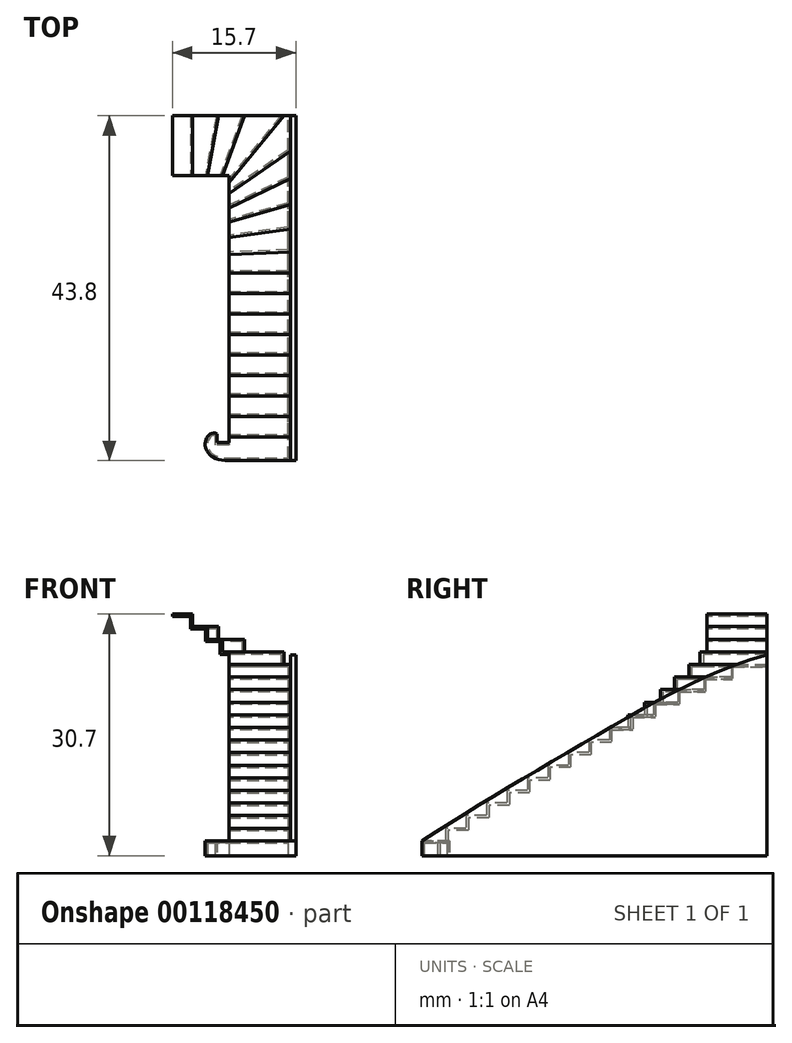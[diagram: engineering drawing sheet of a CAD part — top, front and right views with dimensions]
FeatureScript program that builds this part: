
annotation { "Feature Type Name" : "Feature", "Feature Type Description" : "" }
export const myFeature = defineFeature(function(context is Context, id is Id, definition is map)
    precondition{}
    {
        {
            var Q0;
            Q0=qCreatedBy(makeId("Top.planeOp"),FACE);
            var sketch = newSketch(context, id + "F0", { "sketchPlane" : qUnion([Q0])});
            skLineSegment(sketch, "E0", {"start": v(0, 0) * mm, "end": v(0, -0.9) * mm});
            skLineSegment(sketch, "E1", {"start": v(0, -0.9) * mm, "end": v(0, -2.3) * mm});
            skLineSegment(sketch, "E2", {"start": v(0, -2.3) * mm, "end": v(0, -4.1) * mm});
            skLineSegment(sketch, "E3", {"start": v(0, -4.1) * mm, "end": v(0, -5.9) * mm});
            skLineSegment(sketch, "E4", {"start": v(0, -5.9) * mm, "end": v(0, -7.9) * mm});
            skLineSegment(sketch, "E5", {"start": v(0, -7.9) * mm, "end": v(0, -10) * mm});
            skLineSegment(sketch, "E6", {"start": v(0, -10) * mm, "end": v(0, -12.4) * mm});
            skLineSegment(sketch, "E7", {"start": v(0, -12.4) * mm, "end": v(0, -15) * mm});
            skLineSegment(sketch, "E8", {"start": v(0, -15) * mm, "end": v(7.8, -15) * mm});
            skLineSegment(sketch, "E9", {"start": v(7.8, -15) * mm, "end": v(7.8, -12.4) * mm});
            skLineSegment(sketch, "E10", {"start": v(7.8, -12.4) * mm, "end": v(7.8, -9.7) * mm});
            skLineSegment(sketch, "E11", {"start": v(7.8, -9.7) * mm, "end": v(7.8, -6.8) * mm});
            skLineSegment(sketch, "E12", {"start": v(7.8, -6.8) * mm, "end": v(7.8, -3.7) * mm});
            skLineSegment(sketch, "E13", {"start": v(7.8, -3.7) * mm, "end": v(7.8, -0.4) * mm});
            skLineSegment(sketch, "E14", {"start": v(7.8, -0.4) * mm, "end": v(7.8, 3.1) * mm});
            skLineSegment(sketch, "E15", {"start": v(7.8, 3.1) * mm, "end": v(7.8, 7.6) * mm});
            skLineSegment(sketch, "E16", {"start": v(7.8, 7.6) * mm, "end": v(7, 7.6) * mm});
            skLineSegment(sketch, "E17", {"start": v(7, 7.6) * mm, "end": v(2, 7.6) * mm});
            skLineSegment(sketch, "E18", {"start": v(2, 7.6) * mm, "end": v(-1.3, 7.6) * mm});
            skLineSegment(sketch, "E19", {"start": v(-1.3, 7.6) * mm, "end": v(-4.6, 7.6) * mm});
            skLineSegment(sketch, "E20", {"start": v(-4.6, 7.6) * mm, "end": v(-7.2, 7.6) * mm});
            skLineSegment(sketch, "E21", {"start": v(-7.2, 7.6) * mm, "end": v(-7.2, 0) * mm});
            skLineSegment(sketch, "E22", {"start": v(-7.2, 0) * mm, "end": v(-4.6, 0) * mm});
            skLineSegment(sketch, "E23", {"start": v(-4.6, 0) * mm, "end": v(-2.7, 0) * mm});
            skLineSegment(sketch, "E24", {"start": v(-2.7, 0) * mm, "end": v(-0.8, 0) * mm});
            skLineSegment(sketch, "E25", {"start": v(-0.8, 0) * mm, "end": v(0, 0) * mm});
            skLineSegment(sketch, "E26.0.1.0", {"start": v(0, -17.6) * mm, "end": v(7.8, -17.6) * mm});
            skLineSegment(sketch, "E26.0.1.1", {"start": v(7.8, -17.6) * mm, "end": v(7.8, -15) * mm});
            skLineSegment(sketch, "E26.0.1.2", {"start": v(0, -15) * mm, "end": v(0, -17.6) * mm});
            skLineSegment(sketch, "E26.0.2.0", {"start": v(0, -20.2) * mm, "end": v(7.8, -20.2) * mm});
            skLineSegment(sketch, "E26.0.2.1", {"start": v(7.8, -20.2) * mm, "end": v(7.8, -17.6) * mm});
            skLineSegment(sketch, "E26.0.2.2", {"start": v(0, -17.6) * mm, "end": v(0, -20.2) * mm});
            skLineSegment(sketch, "E26.0.3.0", {"start": v(0, -22.8) * mm, "end": v(7.8, -22.8) * mm});
            skLineSegment(sketch, "E26.0.3.1", {"start": v(7.8, -22.8) * mm, "end": v(7.8, -20.2) * mm});
            skLineSegment(sketch, "E26.0.3.2", {"start": v(0, -20.2) * mm, "end": v(0, -22.8) * mm});
            skLineSegment(sketch, "E26.0.4.0", {"start": v(0, -25.4) * mm, "end": v(7.8, -25.4) * mm});
            skLineSegment(sketch, "E26.0.4.1", {"start": v(7.8, -25.4) * mm, "end": v(7.8, -22.8) * mm});
            skLineSegment(sketch, "E26.0.4.2", {"start": v(0, -22.8) * mm, "end": v(0, -25.4) * mm});
            skLineSegment(sketch, "E26.0.5.0", {"start": v(0, -28) * mm, "end": v(7.8, -28) * mm});
            skLineSegment(sketch, "E26.0.5.1", {"start": v(7.8, -28) * mm, "end": v(7.8, -25.4) * mm});
            skLineSegment(sketch, "E26.0.5.2", {"start": v(0, -25.4) * mm, "end": v(0, -28) * mm});
            skLineSegment(sketch, "E26.0.6.0", {"start": v(0, -30.6) * mm, "end": v(7.8, -30.6) * mm});
            skLineSegment(sketch, "E26.0.6.1", {"start": v(7.8, -30.6) * mm, "end": v(7.8, -28) * mm});
            skLineSegment(sketch, "E26.0.6.2", {"start": v(0, -28) * mm, "end": v(0, -30.6) * mm});
            skLineSegment(sketch, "E26.0.7.0", {"start": v(0, -33.2) * mm, "end": v(7.8, -33.2) * mm});
            skLineSegment(sketch, "E26.0.7.1", {"start": v(7.8, -33.2) * mm, "end": v(7.8, -30.6) * mm});
            skLineSegment(sketch, "E26.0.7.2", {"start": v(0, -30.6) * mm, "end": v(0, -33.2) * mm});
            skLineSegment(sketch, "E26.0.8.0", {"start": v(0, -36.2) * mm, "end": v(7.8, -36.2) * mm});
            skLineSegment(sketch, "E26.0.8.1", {"start": v(7.8, -36.2) * mm, "end": v(7.8, -33.2) * mm});
            skLineSegment(sketch, "E26.0.8.2", {"start": v(0, -33.2) * mm, "end": v(0, -36.2) * mm});
            skLineSegment(sketch, "E26.direction2", {"start": v(0, -15) * mm, "end": v(0, -17.6) * mm, "construction": true});
            skLineSegment(sketch, "E27", {"start": v(7.8, -12.4) * mm, "end": v(0, -12.4) * mm});
            skLineSegment(sketch, "E28", {"start": v(7.8, -9.7) * mm, "end": v(0, -10) * mm});
            skLineSegment(sketch, "E29", {"start": v(7.8, -6.8) * mm, "end": v(0, -7.9) * mm});
            skLineSegment(sketch, "E30", {"start": v(7.8, -3.7) * mm, "end": v(0, -5.9) * mm});
            skLineSegment(sketch, "E31", {"start": v(7.8, -0.4) * mm, "end": v(0, -4.1) * mm});
            skLineSegment(sketch, "E32", {"start": v(7.8, 3.1) * mm, "end": v(0, -2.3) * mm});
            skLineSegment(sketch, "E33", {"start": v(7, 7.6) * mm, "end": v(0, -0.9) * mm});
            skLineSegment(sketch, "E34", {"start": v(2, 7.6) * mm, "end": v(-0.8, 0) * mm});
            skLineSegment(sketch, "E35", {"start": v(-1.3, 7.6) * mm, "end": v(-2.7, 0) * mm});
            skLineSegment(sketch, "E36", {"start": v(-4.6, 7.6) * mm, "end": v(-4.6, 0) * mm});
            skLineSegment(sketch, "E37.bottom", {"start": v(0, -33.2) * mm, "end": v(-1.5, -33.2) * mm, "construction": true});
            skLineSegment(sketch, "E37.top", {"start": v(0, -33.9) * mm, "end": v(-1.5, -33.9) * mm});
            skLineSegment(sketch, "E37.left", {"start": v(0, -33.2) * mm, "end": v(0, -33.9) * mm});
            skLineSegment(sketch, "E37.right", {"start": v(-1.5, -33.2) * mm, "end": v(-1.5, -33.9) * mm});
            skLineSegment(sketch, "E38.bottom", {"start": v(-1.5, -33.2) * mm, "end": v(0, -33.2) * mm, "construction": true});
            skLineSegment(sketch, "E38.top", {"start": v(-1.5, -32.8) * mm, "end": v(0, -32.8) * mm, "construction": true});
            skLineSegment(sketch, "E38.left", {"start": v(-1.5, -33.2) * mm, "end": v(-1.5, -32.8) * mm});
            skLineSegment(sketch, "E38.right", {"start": v(0, -33.2) * mm, "end": v(0, -32.8) * mm, "construction": true});
            skLineSegment(sketch, "E39", {"start": v(0, -33.9) * mm, "end": v(-3, -33.9) * mm, "construction": true});
            skFitSpline(sketch, "E40", {"points": [v(-1.5, -32.8) * mm, v(-3, -33.9) * mm, v(0, -36.2) * mm], "startDerivative": vector(-5.92, 2.61) * mm, "endDerivative": vector(11.96, 0.03) * mm});
            skSolve(sketch);
        }
        {
            var Q0;
            Q0=makeQuery(id+"F0.imprint","IMPRINT",FACE,{"disambiguationData":[TD([[makeQuery(id+"F0.imprint","IMPRINT",EDGE,{"derivedFrom":sQuery(id+"F0.wireOp",EDGE,"E26.0.8.2")}),-1.0]])]});
            var Q1;
            Q1=makeQuery(id+"F0.imprint","IMPRINT",FACE,{"disambiguationData":[TD([[makeQuery(id+"F0.imprint","IMPRINT",EDGE,{"derivedFrom":sQuery(id+"F0.wireOp",EDGE,"E26.0.7.0")}),-1.0]])]});
            extrude(context, id + "F1", {"entities" : qUnion([Q0, Q1]), "depth" : .3 * mm});
        }
        {
            var Q0;
            Q0=makeQuery(id+"F0.imprint","IMPRINT",FACE,{"disambiguationData":[TD([[makeQuery(id+"F0.imprint","IMPRINT",EDGE,{"derivedFrom":sQuery(id+"F0.wireOp",EDGE,"E26.0.6.0")}),-1.0]])]});
            extrude(context, id + "F2", {"entities" : qUnion([Q0]), "operationType" : NewBodyOperationType.ADD, "depth" : 1.9 * mm});
        }
        {
            var Q0;
            Q0=makeQuery(id+"F0.imprint","IMPRINT",FACE,{"disambiguationData":[TD([[makeQuery(id+"F0.imprint","IMPRINT",EDGE,{"derivedFrom":sQuery(id+"F0.wireOp",EDGE,"E26.0.5.0")}),-1.0]])]});
            extrude(context, id + "F3", {"entities" : qUnion([Q0]), "operationType" : NewBodyOperationType.ADD, "depth" : 3.5 * mm});
        }
        {
            var Q0;
            Q0=makeQuery(id+"F0.imprint","IMPRINT",FACE,{"disambiguationData":[TD([[makeQuery(id+"F0.imprint","IMPRINT",EDGE,{"derivedFrom":sQuery(id+"F0.wireOp",EDGE,"E26.0.4.0")}),-1.0]])]});
            extrude(context, id + "F4", {"entities" : qUnion([Q0]), "operationType" : NewBodyOperationType.ADD, "depth" : 5.1 * mm});
        }
        {
            var Q0;
            Q0=makeQuery(id+"F0.imprint","IMPRINT",FACE,{"disambiguationData":[TD([[makeQuery(id+"F0.imprint","IMPRINT",EDGE,{"derivedFrom":sQuery(id+"F0.wireOp",EDGE,"E26.0.3.0")}),-1.0]])]});
            extrude(context, id + "F5", {"entities" : qUnion([Q0]), "operationType" : NewBodyOperationType.ADD, "depth" : 6.7 * mm});
        }
        {
            var Q0;
            Q0=makeQuery(id+"F0.imprint","IMPRINT",FACE,{"disambiguationData":[TD([[makeQuery(id+"F0.imprint","IMPRINT",EDGE,{"derivedFrom":sQuery(id+"F0.wireOp",EDGE,"E26.0.2.0")}),-1.0]])]});
            extrude(context, id + "F6", {"entities" : qUnion([Q0]), "operationType" : NewBodyOperationType.ADD, "depth" : 8.3 * mm});
        }
        {
            var Q0;
            Q0=makeQuery(id+"F0.imprint","IMPRINT",FACE,{"disambiguationData":[TD([[makeQuery(id+"F0.imprint","IMPRINT",EDGE,{"derivedFrom":sQuery(id+"F0.wireOp",EDGE,"E26.0.1.0")}),-1.0]])]});
            extrude(context, id + "F7", {"entities" : qUnion([Q0]), "operationType" : NewBodyOperationType.ADD, "depth" : 9.9 * mm});
        }
        {
            var Q0;
            Q0=makeQuery(id+"F0.imprint","IMPRINT",FACE,{"disambiguationData":[TD([[makeQuery(id+"F0.imprint","IMPRINT",EDGE,{"derivedFrom":sQuery(id+"F0.wireOp",EDGE,"E8")}),-1.0]])]});
            extrude(context, id + "F8", {"entities" : qUnion([Q0]), "operationType" : NewBodyOperationType.ADD, "depth" : 11.5 * mm});
        }
        {
            var Q0;
            Q0=makeQuery(id+"F0.imprint","IMPRINT",FACE,{"disambiguationData":[TD([[makeQuery(id+"F0.imprint","IMPRINT",EDGE,{"derivedFrom":sQuery(id+"F0.wireOp",EDGE,"E7")}),1.0]])]});
            extrude(context, id + "F9", {"entities" : qUnion([Q0]), "operationType" : NewBodyOperationType.ADD, "depth" : 13.1 * mm});
        }
        {
            var Q0;
            Q0=makeQuery(id+"F0.imprint","IMPRINT",FACE,{"disambiguationData":[TD([[makeQuery(id+"F0.imprint","IMPRINT",EDGE,{"derivedFrom":sQuery(id+"F0.wireOp",EDGE,"E6")}),1.0]])]});
            extrude(context, id + "F10", {"entities" : qUnion([Q0]), "operationType" : NewBodyOperationType.ADD, "depth" : 14.7 * mm});
        }
        {
            var Q0;
            Q0=makeQuery(id+"F0.imprint","IMPRINT",FACE,{"disambiguationData":[TD([[makeQuery(id+"F0.imprint","IMPRINT",EDGE,{"derivedFrom":sQuery(id+"F0.wireOp",EDGE,"E5")}),1.0]])]});
            extrude(context, id + "F11", {"entities" : qUnion([Q0]), "operationType" : NewBodyOperationType.ADD, "depth" : 16.3 * mm});
        }
        {
            var Q0;
            Q0=makeQuery(id+"F0.imprint","IMPRINT",FACE,{"disambiguationData":[TD([[makeQuery(id+"F0.imprint","IMPRINT",EDGE,{"derivedFrom":sQuery(id+"F0.wireOp",EDGE,"E4")}),1.0]])]});
            extrude(context, id + "F12", {"entities" : qUnion([Q0]), "operationType" : NewBodyOperationType.ADD, "depth" : 17.9 * mm});
        }
        {
            var Q0;
            Q0=makeQuery(id+"F0.imprint","IMPRINT",FACE,{"disambiguationData":[TD([[makeQuery(id+"F0.imprint","IMPRINT",EDGE,{"derivedFrom":sQuery(id+"F0.wireOp",EDGE,"E3")}),1.0]])]});
            extrude(context, id + "F13", {"entities" : qUnion([Q0]), "operationType" : NewBodyOperationType.ADD, "depth" : 19.5 * mm});
        }
        {
            var Q0;
            Q0=makeQuery(id+"F0.imprint","IMPRINT",FACE,{"disambiguationData":[TD([[makeQuery(id+"F0.imprint","IMPRINT",EDGE,{"derivedFrom":sQuery(id+"F0.wireOp",EDGE,"E2")}),1.0]])]});
            extrude(context, id + "F14", {"entities" : qUnion([Q0]), "operationType" : NewBodyOperationType.ADD, "depth" : 21.1 * mm});
        }
        {
            var Q0;
            Q0=makeQuery(id+"F0.imprint","IMPRINT",FACE,{"disambiguationData":[TD([[makeQuery(id+"F0.imprint","IMPRINT",EDGE,{"derivedFrom":sQuery(id+"F0.wireOp",EDGE,"E1")}),1.0]])]});
            extrude(context, id + "F15", {"entities" : qUnion([Q0]), "operationType" : NewBodyOperationType.ADD, "depth" : 22.7 * mm});
        }
        {
            var Q0;
            Q0=makeQuery(id+"F0.imprint","IMPRINT",FACE,{"disambiguationData":[TD([[makeQuery(id+"F0.imprint","IMPRINT",EDGE,{"derivedFrom":sQuery(id+"F0.wireOp",EDGE,"E0")}),1.0]])]});
            extrude(context, id + "F16", {"entities" : qUnion([Q0]), "operationType" : NewBodyOperationType.ADD, "depth" : 24.3 * mm});
        }
        {
            var Q0;
            Q0=makeQuery(id+"F0.imprint","IMPRINT",FACE,{"disambiguationData":[TD([[makeQuery(id+"F0.imprint","IMPRINT",EDGE,{"derivedFrom":sQuery(id+"F0.wireOp",EDGE,"E18")}),1.0]])]});
            extrude(context, id + "F17", {"entities" : qUnion([Q0]), "operationType" : NewBodyOperationType.ADD, "depth" : 25.9 * mm});
        }
        {
            var Q0;
            Q0=makeQuery(id+"F0.imprint","IMPRINT",FACE,{"disambiguationData":[TD([[makeQuery(id+"F0.imprint","IMPRINT",EDGE,{"derivedFrom":sQuery(id+"F0.wireOp",EDGE,"E19")}),1.0]])]});
            extrude(context, id + "F18", {"entities" : qUnion([Q0]), "operationType" : NewBodyOperationType.ADD, "depth" : 27.5 * mm});
        }
        {
            var Q0;
            Q0=makeQuery(id+"F0.imprint","IMPRINT",FACE,{"disambiguationData":[TD([[makeQuery(id+"F0.imprint","IMPRINT",EDGE,{"derivedFrom":sQuery(id+"F0.wireOp",EDGE,"E20")}),1.0]])]});
            extrude(context, id + "F19", {"entities" : qUnion([Q0]), "operationType" : NewBodyOperationType.ADD, "depth" : 29.1 * mm});
        }
        {
            var Q0;
            Q0 = qSketchRegion(id + "F0", true);
            extrude(context, id + "F20", {"entities" : qUnion([Q0]), "operationType" : NewBodyOperationType.ADD, "oppositeDirection" : true, "depth" : 1.6 * mm});
        }
        {
            var Q0;
            {var subQ0=sQuery(id+"F0.wireOp",EDGE,"E37.left");var subQ1=sQuery(id+"F0.wireOp",EDGE,"E26.0.7.2");var subQ2=sQuery(id+"F0.wireOp",EDGE,"E26.0.6.2");var subQ3=sQuery(id+"F0.wireOp",EDGE,"E26.0.5.2");var subQ4=sQuery(id+"F0.wireOp",EDGE,"E26.0.4.2");var subQ5=sQuery(id+"F0.wireOp",EDGE,"E26.0.3.2");var subQ6=sQuery(id+"F0.wireOp",EDGE,"E26.0.2.2");var subQ7=sQuery(id+"F0.wireOp",EDGE,"E26.0.1.2");var subQ8=sQuery(id+"F0.wireOp",EDGE,"E7");var subQ9=sQuery(id+"F0.wireOp",EDGE,"E6");var subQ10=sQuery(id+"F0.wireOp",EDGE,"E5");var subQ11=sQuery(id+"F0.wireOp",EDGE,"E4");var subQ12=sQuery(id+"F0.wireOp",EDGE,"E3");var subQ13=sQuery(id+"F0.wireOp",EDGE,"E2");var subQ14=sQuery(id+"F0.wireOp",EDGE,"E1");var subQ15=sQuery(id+"F0.wireOp",EDGE,"E0");Q0=makeQuery(id+"F20.boolean.opBoolean","MERGE",FACE,{"derivedFrom":[makeQuery(id+"F16.boolean.opBoolean","MERGE",FACE,{"derivedFrom":[makeQuery(id+"F15.boolean.opBoolean","MERGE",FACE,{"derivedFrom":[makeQuery(id+"F14.boolean.opBoolean","MERGE",FACE,{"derivedFrom":[makeQuery(id+"F13.boolean.opBoolean","MERGE",FACE,{"derivedFrom":[makeQuery(id+"F12.boolean.opBoolean","MERGE",FACE,{"derivedFrom":[makeQuery(id+"F11.boolean.opBoolean","MERGE",FACE,{"derivedFrom":[makeQuery(id+"F10.boolean.opBoolean","MERGE",FACE,{"derivedFrom":[makeQuery(id+"F9.boolean.opBoolean","MERGE",FACE,{"derivedFrom":[makeQuery(id+"F8.boolean.opBoolean","MERGE",FACE,{"derivedFrom":[makeQuery(id+"F7.boolean.opBoolean","MERGE",FACE,{"derivedFrom":[makeQuery(id+"F6.boolean.opBoolean","MERGE",FACE,{"derivedFrom":[makeQuery(id+"F5.boolean.opBoolean","MERGE",FACE,{"derivedFrom":[makeQuery(id+"F4.boolean.opBoolean","MERGE",FACE,{"derivedFrom":[makeQuery(id+"F3.boolean.opBoolean","MERGE",FACE,{"derivedFrom":[makeQuery(id+"F2.boolean.opBoolean","MERGE",FACE,{"derivedFrom":[makeQuery(id+"F1.opExtrude","SWEPT_FACE",FACE,{"disambiguationData":[OSD([subQ0])]}),makeQuery(id+"F2.opExtrude","SWEPT_FACE",FACE,{"disambiguationData":[OSD([subQ1])]})]}),makeQuery(id+"F3.opExtrude","SWEPT_FACE",FACE,{"disambiguationData":[OSD([subQ2])]})]}),makeQuery(id+"F4.opExtrude","SWEPT_FACE",FACE,{"disambiguationData":[OSD([subQ3])]})]}),makeQuery(id+"F5.opExtrude","SWEPT_FACE",FACE,{"disambiguationData":[OSD([subQ4])]})]}),makeQuery(id+"F6.opExtrude","SWEPT_FACE",FACE,{"disambiguationData":[OSD([subQ5])]})]}),makeQuery(id+"F7.opExtrude","SWEPT_FACE",FACE,{"disambiguationData":[OSD([subQ6])]})]}),makeQuery(id+"F8.opExtrude","SWEPT_FACE",FACE,{"disambiguationData":[OSD([subQ7])]})]}),makeQuery(id+"F9.opExtrude","SWEPT_FACE",FACE,{"disambiguationData":[OSD([subQ8])]})]}),makeQuery(id+"F10.opExtrude","SWEPT_FACE",FACE,{"disambiguationData":[OSD([subQ9])]})]}),makeQuery(id+"F11.opExtrude","SWEPT_FACE",FACE,{"disambiguationData":[OSD([subQ10])]})]}),makeQuery(id+"F12.opExtrude","SWEPT_FACE",FACE,{"disambiguationData":[OSD([subQ11])]})]}),makeQuery(id+"F13.opExtrude","SWEPT_FACE",FACE,{"disambiguationData":[OSD([subQ12])]})]}),makeQuery(id+"F14.opExtrude","SWEPT_FACE",FACE,{"disambiguationData":[OSD([subQ13])]})]}),makeQuery(id+"F15.opExtrude","SWEPT_FACE",FACE,{"disambiguationData":[OSD([subQ14])]})]}),makeQuery(id+"F16.opExtrude","SWEPT_FACE",FACE,{"disambiguationData":[OSD([subQ15])]})]}),makeQuery(id+"F20.opExtrude","SWEPT_FACE",FACE,{"disambiguationData":[OSD([subQ15,subQ14,subQ13,subQ12,subQ11,subQ10,subQ9,subQ8,subQ7,subQ6,subQ5,subQ4,subQ3,subQ2,subQ1,subQ0])]})]});}
            var Q1;
            {var subQ0=sQuery(id+"F0.wireOp",EDGE,"E25");var subQ1=sQuery(id+"F0.wireOp",EDGE,"E24");var subQ2=sQuery(id+"F0.wireOp",EDGE,"E23");var subQ3=sQuery(id+"F0.wireOp",EDGE,"E22");Q1=makeQuery(id+"F20.boolean.opBoolean","MERGE",FACE,{"derivedFrom":[makeQuery(id+"F19.boolean.opBoolean","MERGE",FACE,{"derivedFrom":[makeQuery(id+"F18.boolean.opBoolean","MERGE",FACE,{"derivedFrom":[makeQuery(id+"F17.boolean.opBoolean","MERGE",FACE,{"derivedFrom":[makeQuery(id+"F16.opExtrude","SWEPT_FACE",FACE,{"disambiguationData":[OSD([subQ0])]}),makeQuery(id+"F17.opExtrude","SWEPT_FACE",FACE,{"disambiguationData":[OSD([subQ1])]})]}),makeQuery(id+"F18.opExtrude","SWEPT_FACE",FACE,{"disambiguationData":[OSD([subQ2])]})]}),makeQuery(id+"F19.opExtrude","SWEPT_FACE",FACE,{"disambiguationData":[OSD([subQ3])]})]}),makeQuery(id+"F20.opExtrude","SWEPT_FACE",FACE,{"disambiguationData":[OSD([subQ3,subQ2,subQ1,subQ0])]})]});}
            var Q2;
            {var subQ0=sQuery(id+"F0.wireOp",EDGE,"E21");Q2=makeQuery(id+"F20.boolean.opBoolean","MERGE",FACE,{"derivedFrom":[makeQuery(id+"F19.opExtrude","SWEPT_FACE",FACE,{"disambiguationData":[OSD([subQ0])]}),makeQuery(id+"F20.opExtrude","SWEPT_FACE",FACE,{"disambiguationData":[OSD([subQ0])]})]});}
            var Q3;
            Q3=makeQuery(id+"F20.opExtrude","CAP_FACE",FACE,{"disambiguationData":[OSD([sQuery(id+"F0.wireOp",EDGE,"E0"),sQuery(id+"F0.wireOp",EDGE,"E1"),sQuery(id+"F0.wireOp",EDGE,"E2"),sQuery(id+"F0.wireOp",EDGE,"E3"),sQuery(id+"F0.wireOp",EDGE,"E4"),sQuery(id+"F0.wireOp",EDGE,"E5"),sQuery(id+"F0.wireOp",EDGE,"E6"),sQuery(id+"F0.wireOp",EDGE,"E7"),sQuery(id+"F0.wireOp",EDGE,"E9"),sQuery(id+"F0.wireOp",EDGE,"E10"),sQuery(id+"F0.wireOp",EDGE,"E11"),sQuery(id+"F0.wireOp",EDGE,"E12"),sQuery(id+"F0.wireOp",EDGE,"E13"),sQuery(id+"F0.wireOp",EDGE,"E14"),sQuery(id+"F0.wireOp",EDGE,"E15"),sQuery(id+"F0.wireOp",EDGE,"E16"),sQuery(id+"F0.wireOp",EDGE,"E17"),sQuery(id+"F0.wireOp",EDGE,"E18"),sQuery(id+"F0.wireOp",EDGE,"E19"),sQuery(id+"F0.wireOp",EDGE,"E20"),sQuery(id+"F0.wireOp",EDGE,"E21"),sQuery(id+"F0.wireOp",EDGE,"E22"),sQuery(id+"F0.wireOp",EDGE,"E23"),sQuery(id+"F0.wireOp",EDGE,"E24"),sQuery(id+"F0.wireOp",EDGE,"E25"),sQuery(id+"F0.wireOp",EDGE,"E26.0.1.1"),sQuery(id+"F0.wireOp",EDGE,"E26.0.1.2"),sQuery(id+"F0.wireOp",EDGE,"E26.0.2.1"),sQuery(id+"F0.wireOp",EDGE,"E26.0.2.2"),sQuery(id+"F0.wireOp",EDGE,"E26.0.3.1"),sQuery(id+"F0.wireOp",EDGE,"E26.0.3.2"),sQuery(id+"F0.wireOp",EDGE,"E26.0.4.1"),sQuery(id+"F0.wireOp",EDGE,"E26.0.4.2"),sQuery(id+"F0.wireOp",EDGE,"E26.0.5.1"),sQuery(id+"F0.wireOp",EDGE,"E26.0.5.2"),sQuery(id+"F0.wireOp",EDGE,"E26.0.6.1"),sQuery(id+"F0.wireOp",EDGE,"E26.0.6.2"),sQuery(id+"F0.wireOp",EDGE,"E26.0.7.1"),sQuery(id+"F0.wireOp",EDGE,"E26.0.7.2"),sQuery(id+"F0.wireOp",EDGE,"E26.0.8.0"),sQuery(id+"F0.wireOp",EDGE,"E26.0.8.1"),sQuery(id+"F0.wireOp",EDGE,"E37.top"),sQuery(id+"F0.wireOp",EDGE,"E37.left"),sQuery(id+"F0.wireOp",EDGE,"E37.right"),sQuery(id+"F0.wireOp",EDGE,"E38.left"),sQuery(id+"F0.wireOp",EDGE,"E40")])],"isStart":false});
            var Q4;
            {var subQ0=sQuery(id+"F0.wireOp",EDGE,"E20");var subQ1=sQuery(id+"F0.wireOp",EDGE,"E19");var subQ2=sQuery(id+"F0.wireOp",EDGE,"E18");var subQ3=sQuery(id+"F0.wireOp",EDGE,"E17");var subQ4=sQuery(id+"F0.wireOp",EDGE,"E16");Q4=makeQuery(id+"F20.boolean.opBoolean","MERGE",FACE,{"derivedFrom":[makeQuery(id+"F19.boolean.opBoolean","MERGE",FACE,{"derivedFrom":[makeQuery(id+"F18.boolean.opBoolean","MERGE",FACE,{"derivedFrom":[makeQuery(id+"F17.boolean.opBoolean","MERGE",FACE,{"derivedFrom":[makeQuery(id+"F16.boolean.opBoolean","MERGE",FACE,{"derivedFrom":[makeQuery(id+"F15.opExtrude","SWEPT_FACE",FACE,{"disambiguationData":[OSD([subQ4])]}),makeQuery(id+"F16.opExtrude","SWEPT_FACE",FACE,{"disambiguationData":[OSD([subQ3])]})]}),makeQuery(id+"F17.opExtrude","SWEPT_FACE",FACE,{"disambiguationData":[OSD([subQ2])]})]}),makeQuery(id+"F18.opExtrude","SWEPT_FACE",FACE,{"disambiguationData":[OSD([subQ1])]})]}),makeQuery(id+"F19.opExtrude","SWEPT_FACE",FACE,{"disambiguationData":[OSD([subQ0])]})]}),makeQuery(id+"F20.opExtrude","SWEPT_FACE",FACE,{"disambiguationData":[OSD([subQ4,subQ3,subQ2,subQ1,subQ0])]})]});}
            shell(context, id + "F21", {"entities" : qUnion([Q0, Q1, Q2, Q3, Q4]), "thickness" : .3 * mm});
        }
        {
            var Q0;
            {var subQ0=sQuery(id+"F0.wireOp",EDGE,"E26.0.8.1");var subQ1=sQuery(id+"F0.wireOp",EDGE,"E26.0.7.1");var subQ2=sQuery(id+"F0.wireOp",EDGE,"E26.0.6.1");var subQ3=sQuery(id+"F0.wireOp",EDGE,"E26.0.5.1");var subQ4=sQuery(id+"F0.wireOp",EDGE,"E26.0.4.1");var subQ5=sQuery(id+"F0.wireOp",EDGE,"E26.0.3.1");var subQ6=sQuery(id+"F0.wireOp",EDGE,"E26.0.2.1");var subQ7=sQuery(id+"F0.wireOp",EDGE,"E26.0.1.1");var subQ8=sQuery(id+"F0.wireOp",EDGE,"E15");var subQ9=sQuery(id+"F0.wireOp",EDGE,"E14");var subQ10=sQuery(id+"F0.wireOp",EDGE,"E13");var subQ11=sQuery(id+"F0.wireOp",EDGE,"E12");var subQ12=sQuery(id+"F0.wireOp",EDGE,"E11");var subQ13=sQuery(id+"F0.wireOp",EDGE,"E10");var subQ14=sQuery(id+"F0.wireOp",EDGE,"E9");Q0=makeQuery(id+"F20.boolean.opBoolean","MERGE",FACE,{"derivedFrom":[makeQuery(id+"F15.boolean.opBoolean","MERGE",FACE,{"derivedFrom":[makeQuery(id+"F14.boolean.opBoolean","MERGE",FACE,{"derivedFrom":[makeQuery(id+"F13.boolean.opBoolean","MERGE",FACE,{"derivedFrom":[makeQuery(id+"F12.boolean.opBoolean","MERGE",FACE,{"derivedFrom":[makeQuery(id+"F11.boolean.opBoolean","MERGE",FACE,{"derivedFrom":[makeQuery(id+"F10.boolean.opBoolean","MERGE",FACE,{"derivedFrom":[makeQuery(id+"F9.boolean.opBoolean","MERGE",FACE,{"derivedFrom":[makeQuery(id+"F8.boolean.opBoolean","MERGE",FACE,{"derivedFrom":[makeQuery(id+"F7.boolean.opBoolean","MERGE",FACE,{"derivedFrom":[makeQuery(id+"F6.boolean.opBoolean","MERGE",FACE,{"derivedFrom":[makeQuery(id+"F5.boolean.opBoolean","MERGE",FACE,{"derivedFrom":[makeQuery(id+"F4.boolean.opBoolean","MERGE",FACE,{"derivedFrom":[makeQuery(id+"F3.boolean.opBoolean","MERGE",FACE,{"derivedFrom":[makeQuery(id+"F2.boolean.opBoolean","MERGE",FACE,{"derivedFrom":[makeQuery(id+"F1.opExtrude","SWEPT_FACE",FACE,{"disambiguationData":[OSD([subQ0])]}),makeQuery(id+"F2.opExtrude","SWEPT_FACE",FACE,{"disambiguationData":[OSD([subQ1])]})]}),makeQuery(id+"F3.opExtrude","SWEPT_FACE",FACE,{"disambiguationData":[OSD([subQ2])]})]}),makeQuery(id+"F4.opExtrude","SWEPT_FACE",FACE,{"disambiguationData":[OSD([subQ3])]})]}),makeQuery(id+"F5.opExtrude","SWEPT_FACE",FACE,{"disambiguationData":[OSD([subQ4])]})]}),makeQuery(id+"F6.opExtrude","SWEPT_FACE",FACE,{"disambiguationData":[OSD([subQ5])]})]}),makeQuery(id+"F7.opExtrude","SWEPT_FACE",FACE,{"disambiguationData":[OSD([subQ6])]})]}),makeQuery(id+"F8.opExtrude","SWEPT_FACE",FACE,{"disambiguationData":[OSD([subQ7])]})]}),makeQuery(id+"F9.opExtrude","SWEPT_FACE",FACE,{"disambiguationData":[OSD([subQ14])]})]}),makeQuery(id+"F10.opExtrude","SWEPT_FACE",FACE,{"disambiguationData":[OSD([subQ13])]})]}),makeQuery(id+"F11.opExtrude","SWEPT_FACE",FACE,{"disambiguationData":[OSD([subQ12])]})]}),makeQuery(id+"F12.opExtrude","SWEPT_FACE",FACE,{"disambiguationData":[OSD([subQ11])]})]}),makeQuery(id+"F13.opExtrude","SWEPT_FACE",FACE,{"disambiguationData":[OSD([subQ10])]})]}),makeQuery(id+"F14.opExtrude","SWEPT_FACE",FACE,{"disambiguationData":[OSD([subQ9])]})]}),makeQuery(id+"F15.opExtrude","SWEPT_FACE",FACE,{"disambiguationData":[OSD([subQ8])]})]}),makeQuery(id+"F20.opExtrude","SWEPT_FACE",FACE,{"disambiguationData":[OSD([subQ14,subQ13,subQ12,subQ11,subQ10,subQ9,subQ8,subQ7,subQ6,subQ5,subQ4,subQ3,subQ2,subQ1,subQ0])]})]});}
            var sketch = newSketch(context, id + "F22", { "sketchPlane" : qUnion([Q0])});
            skLineSegment(sketch, "E41", {"start": v(7.6, 22.7) * mm, "end": v(7.6, 23.9) * mm, "construction": true});
            skFitSpline(sketch, "E42", {"points": [v(-36.2, 0.3) * mm, v(-15, 13.1) * mm, v(7.6, 23.9) * mm], "startDerivative": vector(41.77, 26.84) * mm, "endDerivative": vector(45.47, 11.97) * mm});
            skPoint(sketch, "E43", {"position": v(3.1, 21.9) * mm});
            skLineSegment(sketch, "E44", {"start": v(7.6, 23.9) * mm, "end": v(7.6, -1.6) * mm});
            skLineSegment(sketch, "E45", {"start": v(7.6, -1.6) * mm, "end": v(-36.2, -1.6) * mm});
            skLineSegment(sketch, "E46", {"start": v(-36.2, -1.6) * mm, "end": v(-36.2, 0.3) * mm});
            skSolve(sketch);
        }
        {
            var Q0;
            Q0 = qSketchRegion(id + "F22", true);
            extrude(context, id + "F23", {"entities" : qUnion([Q0]), "operationType" : NewBodyOperationType.ADD, "depth" : .7 * mm});
        }
    });
